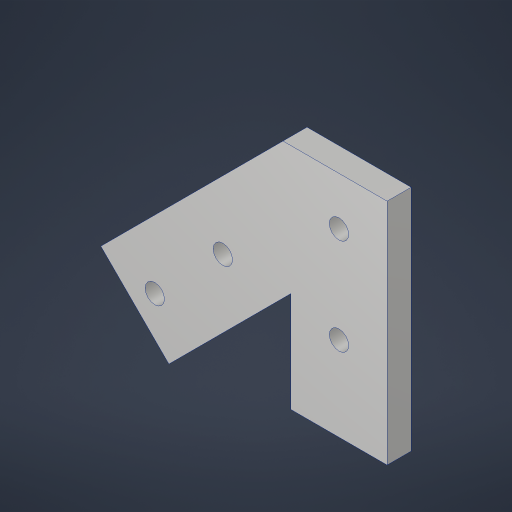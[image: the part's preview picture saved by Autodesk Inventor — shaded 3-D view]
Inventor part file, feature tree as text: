
AUTODESK INVENTOR PART (.ipt)
format: ipt  version: 2023.4 (Build 274418000, 418)  size: 192,000 bytes
history: native  units: in
note: dims shown in document units (in); Inventor stores cm internally (conversion verified against a paired STEP export)
features: sketch x2, projected_geometry x2, extrude x1, hole x1
ambient origin geometry x8: Origin, YZ Plane, XZ Plane, XY Plane, X Axis, Y Axis, Z Axis, Center Point
bodies: Solid1 (feature_tree)
feature tree (6):
  extrude  "Extrusion1"  Depth=2.25in
  hole  "Hole1"  [1 undecoded]
  sketch  "Sketch1"  dims[d0=45.0deg d1=2.25in]
  sketch  "Sketch2"  dims[d2=3.0in d3=0.125in d4=1.0in d5=1.0in d6=0.25in d7=0.0in d8=1.0in d9=1.0in d12=0.201in d13=0.75in d14=0.385in d15=0.25in d16=0.5635in d17=1.0in d18=0.8108in d19=0.5in d21=1.0in]
  projected_geometry  "Project Cut Edges1"
  projected_geometry  "Project Cut Edges2"
note: 1 required parameter value undecoded (feature->parameter linkage not recoverable at this tier; creation-order binding heuristic only, values carry confidence <= 0.55)
